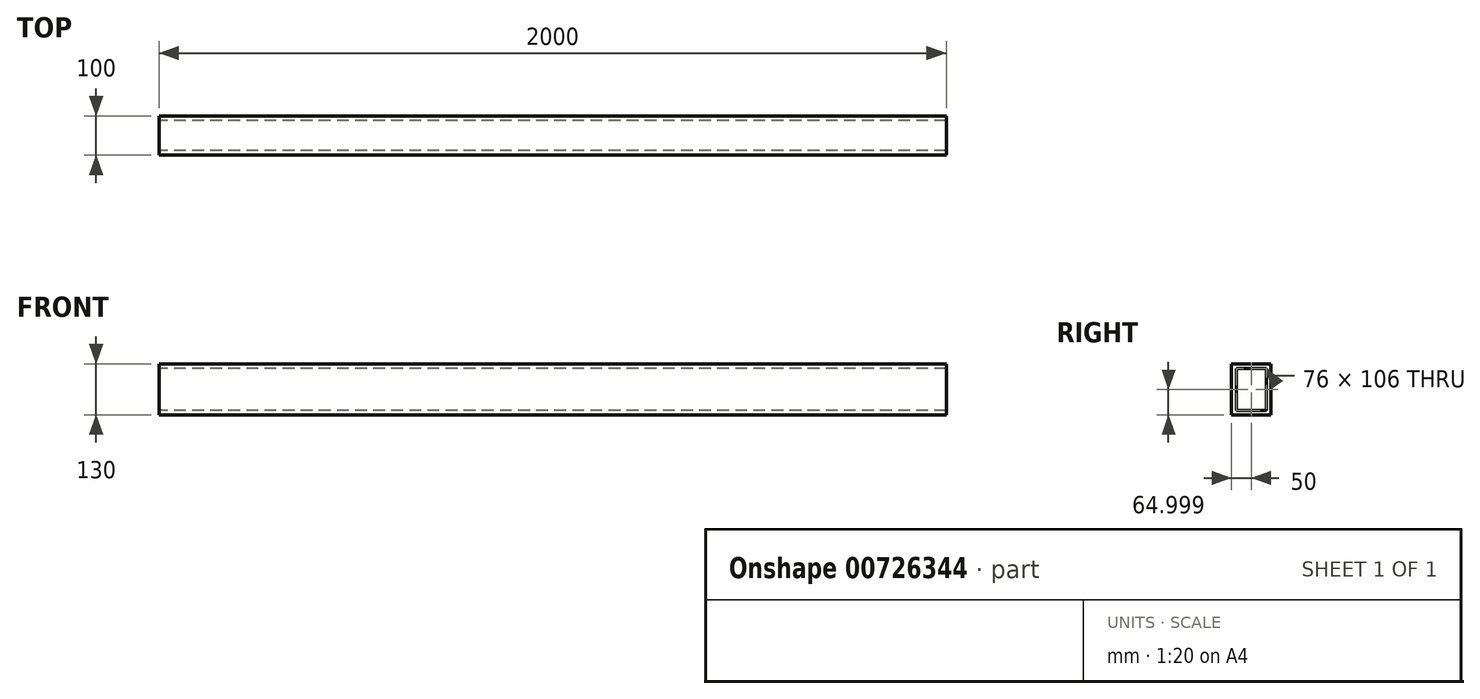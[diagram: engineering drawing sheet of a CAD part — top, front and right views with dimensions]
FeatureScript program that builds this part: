
annotation { "Feature Type Name" : "Feature", "Feature Type Description" : "" }
export const myFeature = defineFeature(function(context is Context, id is Id, definition is map)
    precondition{}
    {
        {
            var Q0;
            Q0=qCreatedBy(makeId("Front.planeOp"),FACE);
            var sketch = newSketch(context, id + "F0", { "sketchPlane" : qUnion([Q0])});
            skLineSegment(sketch, "E0.bottom", {"start": v(-1001.15, -50.5) * mm, "end": v(998.85, -50.5) * mm});
            skLineSegment(sketch, "E0.top", {"start": v(-1001.15, -180.5) * mm, "end": v(998.85, -180.5) * mm});
            skLineSegment(sketch, "E0.left", {"start": v(-1001.15, -50.5) * mm, "end": v(-1001.15, -180.5) * mm});
            skLineSegment(sketch, "E0.right", {"start": v(998.85, -50.5) * mm, "end": v(998.85, -180.5) * mm});
            skSolve(sketch);
        }
        {
            var Q0;
            Q0 = qSketchRegion(id + "F0", true);
            extrude(context, id + "F1", {"entities" : qUnion([Q0]), "depth" : 100 * mm, "offsetDistance" : 25 * mm});
        }
        {
            var Q0;
            Q0=makeQuery(id+"F1.opExtrude","SWEPT_FACE",FACE,{"disambiguationData":[OSD([sQuery(id+"F0.wireOp",EDGE,"E0.left")])]});
            var sketch = newSketch(context, id + "F2", { "sketchPlane" : qUnion([Q0])});
            skLineSegment(sketch, "E1.bottom", {"start": v(12, -62.5) * mm, "end": v(88, -62.5) * mm});
            skLineSegment(sketch, "E1.top", {"start": v(12, -168.5) * mm, "end": v(88, -168.5) * mm});
            skLineSegment(sketch, "E1.left", {"start": v(12, -62.5) * mm, "end": v(12, -168.5) * mm});
            skLineSegment(sketch, "E1.right", {"start": v(88, -62.5) * mm, "end": v(88, -168.5) * mm});
            skSolve(sketch);
        }
        {
            var Q0;
            Q0 = qSketchRegion(id + "F2", true);
            extrude(context, id + "F3", {"entities" : qUnion([Q0]), "operationType" : NewBodyOperationType.REMOVE, "oppositeDirection" : true, "depth" : 2000 * mm, "offsetDistance" : 25 * mm});
        }
    });
